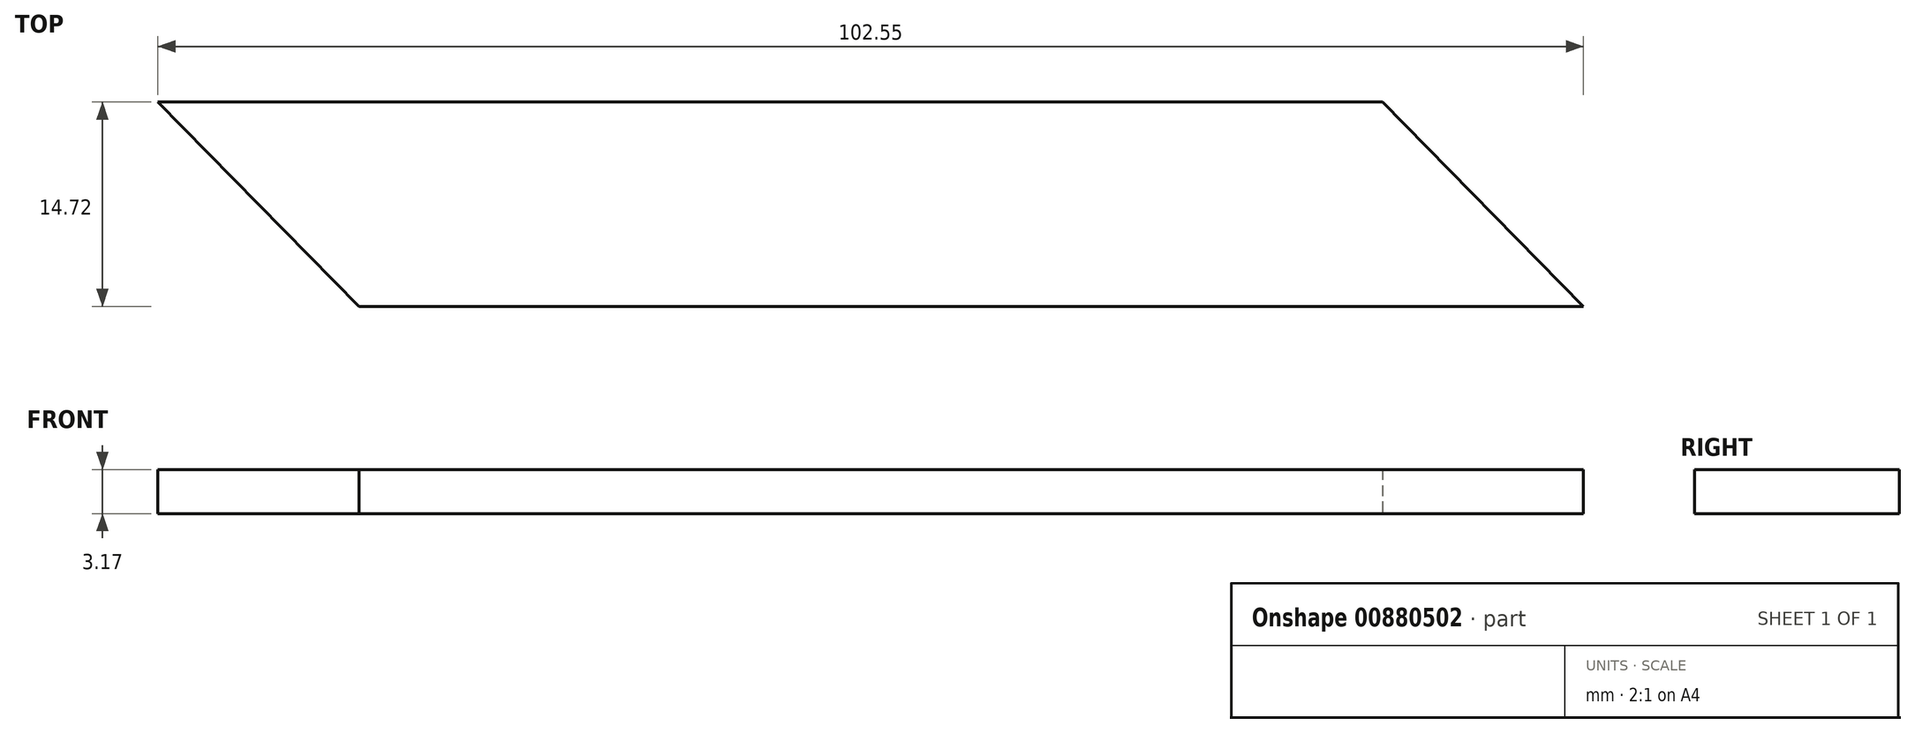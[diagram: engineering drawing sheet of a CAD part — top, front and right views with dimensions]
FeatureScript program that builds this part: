
annotation { "Feature Type Name" : "Feature", "Feature Type Description" : "" }
export const myFeature = defineFeature(function(context is Context, id is Id, definition is map)
    precondition{}
    {
        {
            var Q0;
            Q0=qCreatedBy(makeId("Top.planeOp"), FACE);
            var sketch = newSketch(context, id + "F0", { "sketchPlane" : qUnion([Q0])});
            skLineSegment(sketch, "E0", {"start": v(-33.62, 26.67) * mm, "end": v(54.46, 26.67) * mm});
            skLineSegment(sketch, "E1", {"start": v(54.46, 26.67) * mm, "end": v(68.93, 11.95) * mm});
            skLineSegment(sketch, "E2", {"start": v(-33.62, 26.67) * mm, "end": v(-19.16, 11.95) * mm});
            skLineSegment(sketch, "E3", {"start": v(68.93, 11.95) * mm, "end": v(-19.16, 11.95) * mm});
            skSolve(sketch);
        }
        {
            var Q0;
            Q0 = qSketchRegion(id + "F0", true);
            extrude(context, id + "F1", {"entities" : qUnion([Q0]), "domain" : OperationDomain.MODEL, "flatOperationType" : FlatOperationType.REMOVE, "depth" : 3.17 * mm, "offsetDistance" : 25.4 * mm});
        }
    });
